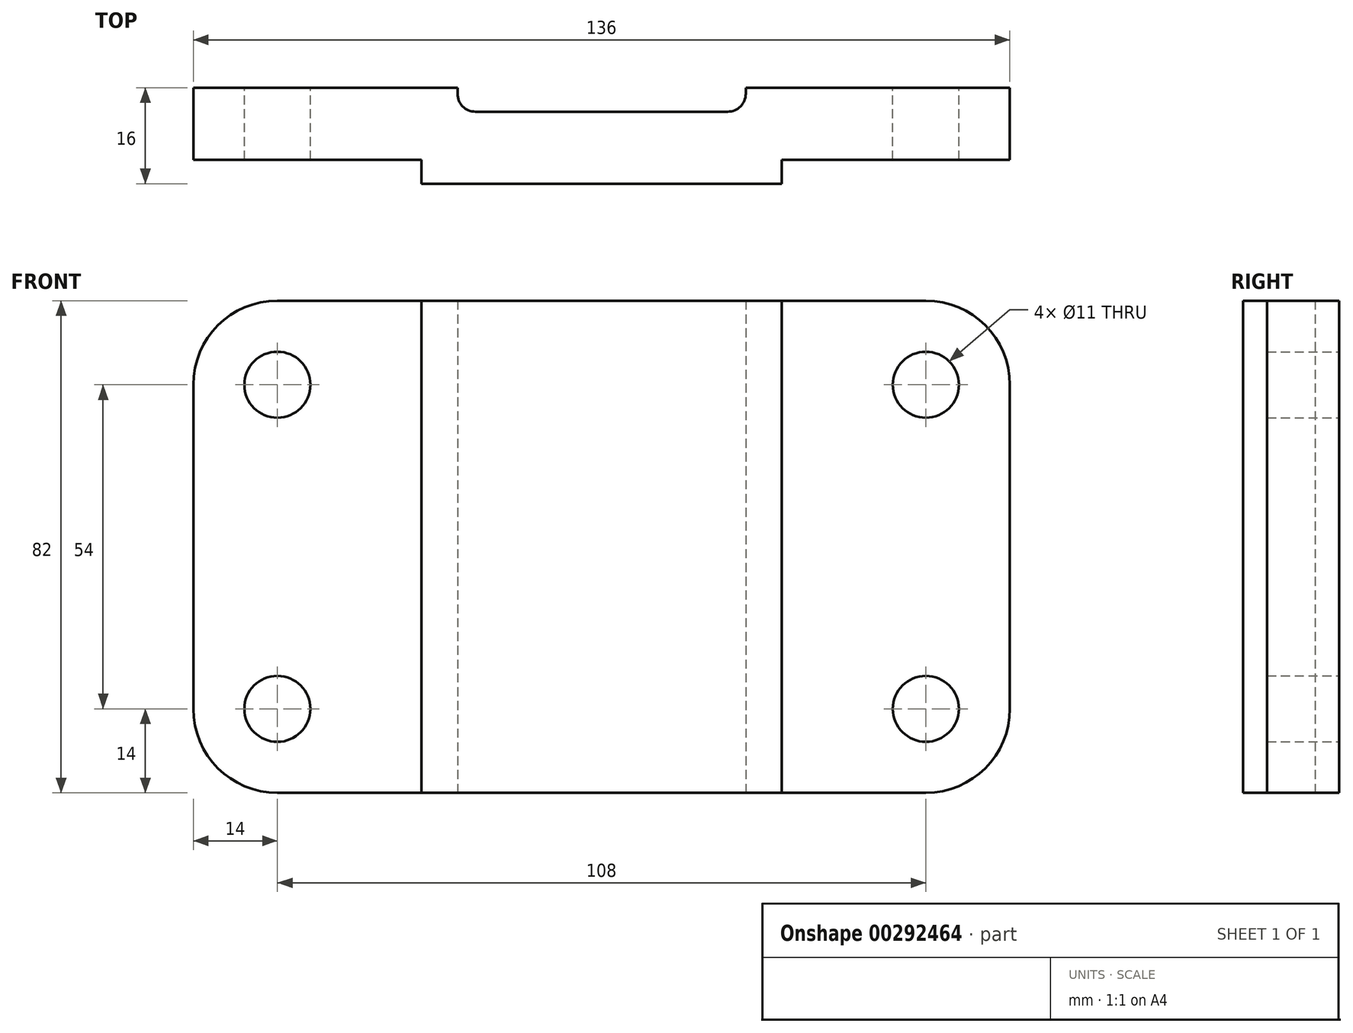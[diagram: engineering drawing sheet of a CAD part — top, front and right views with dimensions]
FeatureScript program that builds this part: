
annotation { "Feature Type Name" : "Feature", "Feature Type Description" : "" }
export const myFeature = defineFeature(function(context is Context, id is Id, definition is map)
    precondition{}
    {
        {
            var Q0;
            Q0=qCreatedBy(makeId("Front.planeOp"),FACE);
            var sketch = newSketch(context, id + "F0", { "sketchPlane" : qUnion([Q0])});
            skLineSegment(sketch, "E0.bottom", {"start": v(14, 0) * mm, "end": v(122, 0) * mm});
            skLineSegment(sketch, "E0.top", {"start": v(14, 82) * mm, "end": v(122, 82) * mm});
            skLineSegment(sketch, "E0.left", {"start": v(0, 14) * mm, "end": v(0, 68) * mm});
            skLineSegment(sketch, "E0.right", {"start": v(136, 14) * mm, "end": v(136, 68) * mm});
            skPoint(sketch, "E1.visualSharp", {"position": v(0, 82) * mm});
            skArc(sketch, "E1.filletArc", {"start": v(14, 82) * mm, "mid": v(4.1, 77.9) * mm, "end": v(0, 68) * mm});
            skPoint(sketch, "E2.visualSharp", {"position": v(0, 0) * mm});
            skArc(sketch, "E2.filletArc", {"start": v(0, 14) * mm, "mid": v(4.1, 4.1) * mm, "end": v(14, 0) * mm});
            skPoint(sketch, "E3.visualSharp", {"position": v(136, 82) * mm});
            skArc(sketch, "E3.filletArc", {"start": v(136, 68) * mm, "mid": v(131.9, 77.9) * mm, "end": v(122, 82) * mm});
            skPoint(sketch, "E4.visualSharp", {"position": v(136, 0) * mm});
            skArc(sketch, "E4.filletArc", {"start": v(122, 0) * mm, "mid": v(131.9, 4.1) * mm, "end": v(136, 14) * mm});
            skCircle(sketch, "E5", {"center": v(14, 68) * mm, "radius": 5.5 * mm});
            skCircle(sketch, "E6", {"center": v(14, 14) * mm, "radius": 5.5 * mm});
            skCircle(sketch, "E7", {"center": v(122, 14) * mm, "radius": 5.5 * mm});
            skCircle(sketch, "E8", {"center": v(122, 68) * mm, "radius": 5.5 * mm});
            skSolve(sketch);
        }
        {
            var Q0;
            Q0 = qSketchRegion(id + "F0", true);
            extrude(context, id + "F1", {"entities" : qUnion([Q0]), "depth" : 16 * mm});
        }
        {
            var Q0;
            Q0=qCreatedBy(makeId("Top.planeOp"),FACE);
            var sketch = newSketch(context, id + "F2", { "sketchPlane" : qUnion([Q0])});
            skLineSegment(sketch, "E9.bottom", {"start": v(0, -16) * mm, "end": v(38, -16) * mm});
            skLineSegment(sketch, "E9.top", {"start": v(0, -12) * mm, "end": v(38, -12) * mm});
            skLineSegment(sketch, "E9.left", {"start": v(0, -16) * mm, "end": v(0, -12) * mm});
            skLineSegment(sketch, "E9.right", {"start": v(38, -16) * mm, "end": v(38, -12) * mm});
            skLineSegment(sketch, "E10.bottom", {"start": v(136, -16) * mm, "end": v(98, -16) * mm});
            skLineSegment(sketch, "E10.top", {"start": v(136, -12) * mm, "end": v(98, -12) * mm});
            skLineSegment(sketch, "E10.left", {"start": v(136, -16) * mm, "end": v(136, -12) * mm});
            skLineSegment(sketch, "E10.right", {"start": v(98, -16) * mm, "end": v(98, -12) * mm});
            skSolve(sketch);
        }
        {
            var Q0;
            Q0 = qSketchRegion(id + "F2", true);
            extrude(context, id + "F3", {"entities" : qUnion([Q0]), "operationType" : NewBodyOperationType.REMOVE, "endBound" : BoundingType.THROUGH_ALL, "depth" : 25 * mm});
        }
        {
            var Q0;
            Q0=qCreatedBy(makeId("Top.planeOp"),FACE);
            var sketch = newSketch(context, id + "F4", { "sketchPlane" : qUnion([Q0])});
            skLineSegment(sketch, "E11.bottom", {"start": v(44, 0) * mm, "end": v(92, 0) * mm});
            skLineSegment(sketch, "E11.top", {"start": v(47, -4) * mm, "end": v(89, -4) * mm});
            skLineSegment(sketch, "E11.left", {"start": v(44, 0) * mm, "end": v(44, -1) * mm});
            skLineSegment(sketch, "E11.right", {"start": v(92, 0) * mm, "end": v(92, -1) * mm});
            skPoint(sketch, "E12.visualSharp", {"position": v(44, -4) * mm});
            skArc(sketch, "E12.filletArc", {"start": v(44, -1) * mm, "mid": v(44.88, -3.12) * mm, "end": v(47, -4) * mm});
            skPoint(sketch, "E13.visualSharp", {"position": v(92, -4) * mm});
            skArc(sketch, "E13.filletArc", {"start": v(89, -4) * mm, "mid": v(91.12, -3.12) * mm, "end": v(92, -1) * mm});
            skSolve(sketch);
        }
        {
            var Q0;
            Q0 = qSketchRegion(id + "F4", true);
            extrude(context, id + "F5", {"entities" : qUnion([Q0]), "operationType" : NewBodyOperationType.REMOVE, "endBound" : BoundingType.THROUGH_ALL, "depth" : 25 * mm});
        }
    });
